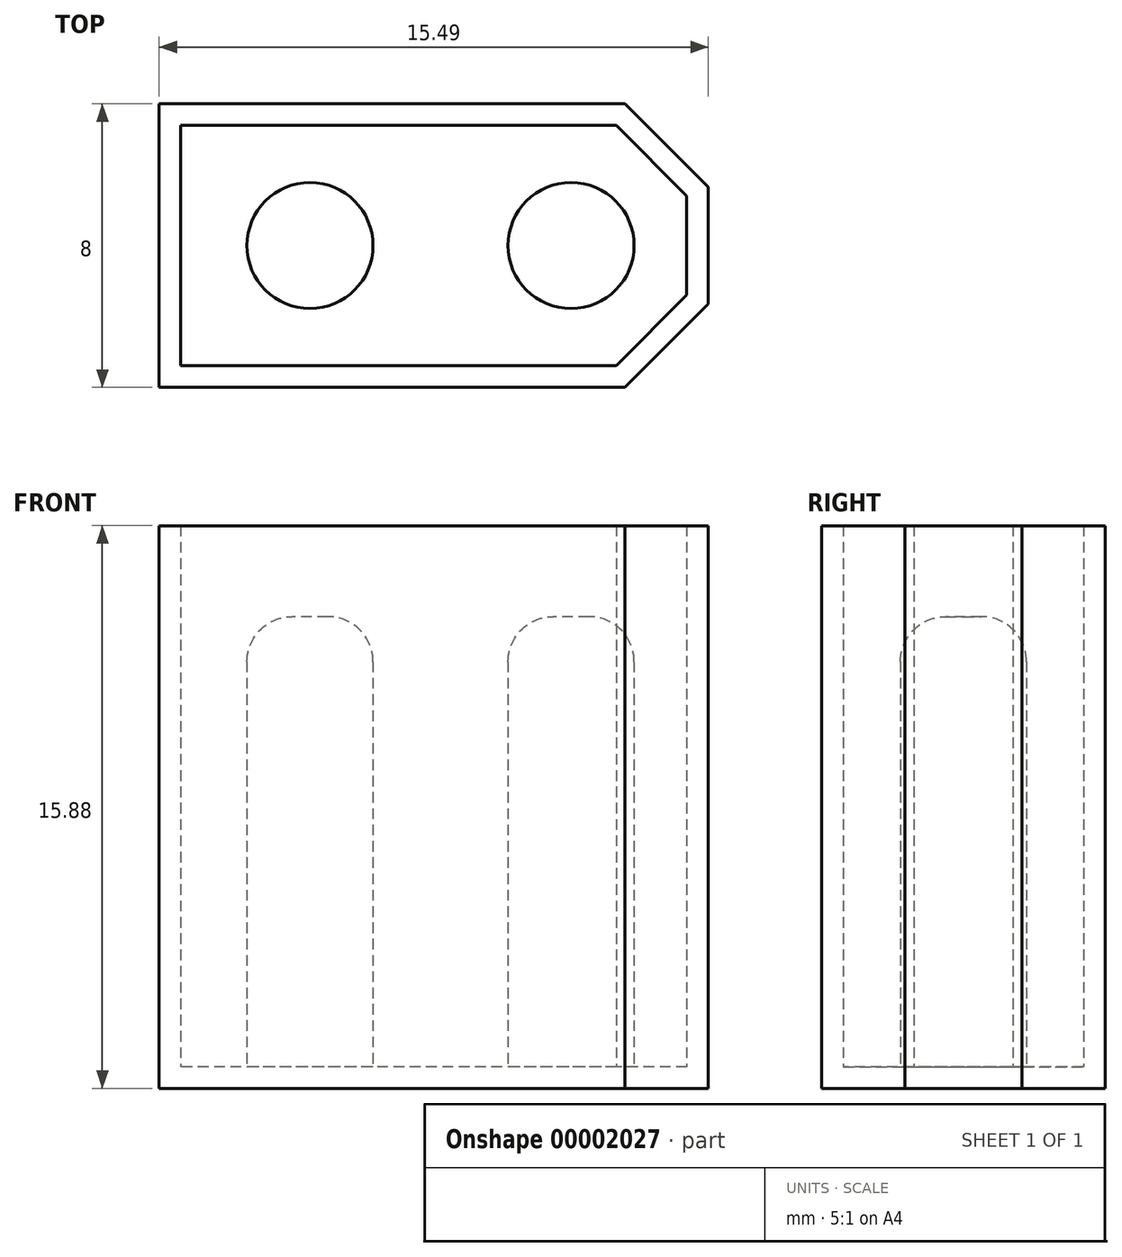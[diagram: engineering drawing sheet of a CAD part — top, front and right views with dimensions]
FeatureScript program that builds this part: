
annotation { "Feature Type Name" : "Feature", "Feature Type Description" : "" }
export const myFeature = defineFeature(function(context is Context, id is Id, definition is map)
    precondition{}
    {
        {
            var Q0;
            Q0=qCreatedBy(makeId("Top.planeOp"),FACE);
            var sketch = newSketch(context, id + "F0", { "sketchPlane" : qUnion([Q0])});
            skLineSegment(sketch, "E0", {"start": v(0, -4) * mm, "end": v(0, 4) * mm});
            skLineSegment(sketch, "E1", {"start": v(0, 4) * mm, "end": v(13.14, 4) * mm});
            skLineSegment(sketch, "E2", {"start": v(13.14, 4) * mm, "end": v(15.5, 1.65) * mm});
            skLineSegment(sketch, "E3", {"start": v(15.5, 1.65) * mm, "end": v(15.5, -1.65) * mm});
            skLineSegment(sketch, "E4", {"start": v(15.5, -1.65) * mm, "end": v(13.14, -4) * mm});
            skLineSegment(sketch, "E5", {"start": v(13.14, -4) * mm, "end": v(0, -4) * mm});
            skSolve(sketch);
        }
        {
            var Q0;
            Q0 = qSketchRegion(id + "F0", true);
            extrude(context, id + "F1", {"entities" : qUnion([Q0]), "depth" : 15.88 * mm});
        }
        {
            var Q0;
            Q0=makeQuery(id+"F1.opExtrude","CAP_FACE",FACE,{"disambiguationData":[OSD([sQuery(id+"F0.wireOp",EDGE,"E0"),sQuery(id+"F0.wireOp",EDGE,"E1"),sQuery(id+"F0.wireOp",EDGE,"E2"),sQuery(id+"F0.wireOp",EDGE,"E3"),sQuery(id+"F0.wireOp",EDGE,"E4"),sQuery(id+"F0.wireOp",EDGE,"E5")])],"isStart":false});
            shell(context, id + "F2", {"entities" : qUnion([Q0]), "thickness" : 0.6 * mm});
        }
        {
            var Q0;
            Q0=makeQuery(id+"F2.opShell","OFFSET_FACE",FACE,{"disambiguationData":[OSD([sQuery(id+"F0.wireOp",EDGE,"E0"),sQuery(id+"F0.wireOp",EDGE,"E1"),sQuery(id+"F0.wireOp",EDGE,"E2"),sQuery(id+"F0.wireOp",EDGE,"E3"),sQuery(id+"F0.wireOp",EDGE,"E4"),sQuery(id+"F0.wireOp",EDGE,"E5")])]});
            var sketch = newSketch(context, id + "F3", { "sketchPlane" : qUnion([Q0])});
            skCircle(sketch, "E6", {"center": v(11.62, 0) * mm, "radius": 1.78 * mm});
            skCircle(sketch, "E7", {"center": v(4.25, 0) * mm, "radius": 1.78 * mm});
            skLineSegment(sketch, "E8", {"start": v(4.25, 0) * mm, "end": v(11.62, 0) * mm, "construction": true});
            skSolve(sketch);
        }
        {
            var Q0;
            Q0 = qSketchRegion(id + "F3", true);
            extrude(context, id + "F4", {"entities" : qUnion([Q0]), "operationType" : NewBodyOperationType.ADD, "depth" : 12.7 * mm});
        }
        {
            var Q0;
            Q0=makeQuery(id+"F4.opExtrude","CAP_EDGE",EDGE,{"disambiguationData":[OSD([sQuery(id+"F3.wireOp",EDGE,"E7")])],"isStart":false});
            var Q1;
            Q1=makeQuery(id+"F4.opExtrude","CAP_EDGE",EDGE,{"disambiguationData":[OSD([sQuery(id+"F3.wireOp",EDGE,"E6")])],"isStart":false});
            fillet(context, id + "F5", {"entities" : qUnion([Q0, Q1]), "radius" : 1.27 * mm, "tangentPropagation" : true, "allowEdgeOverflow" : false});
        }
    });
